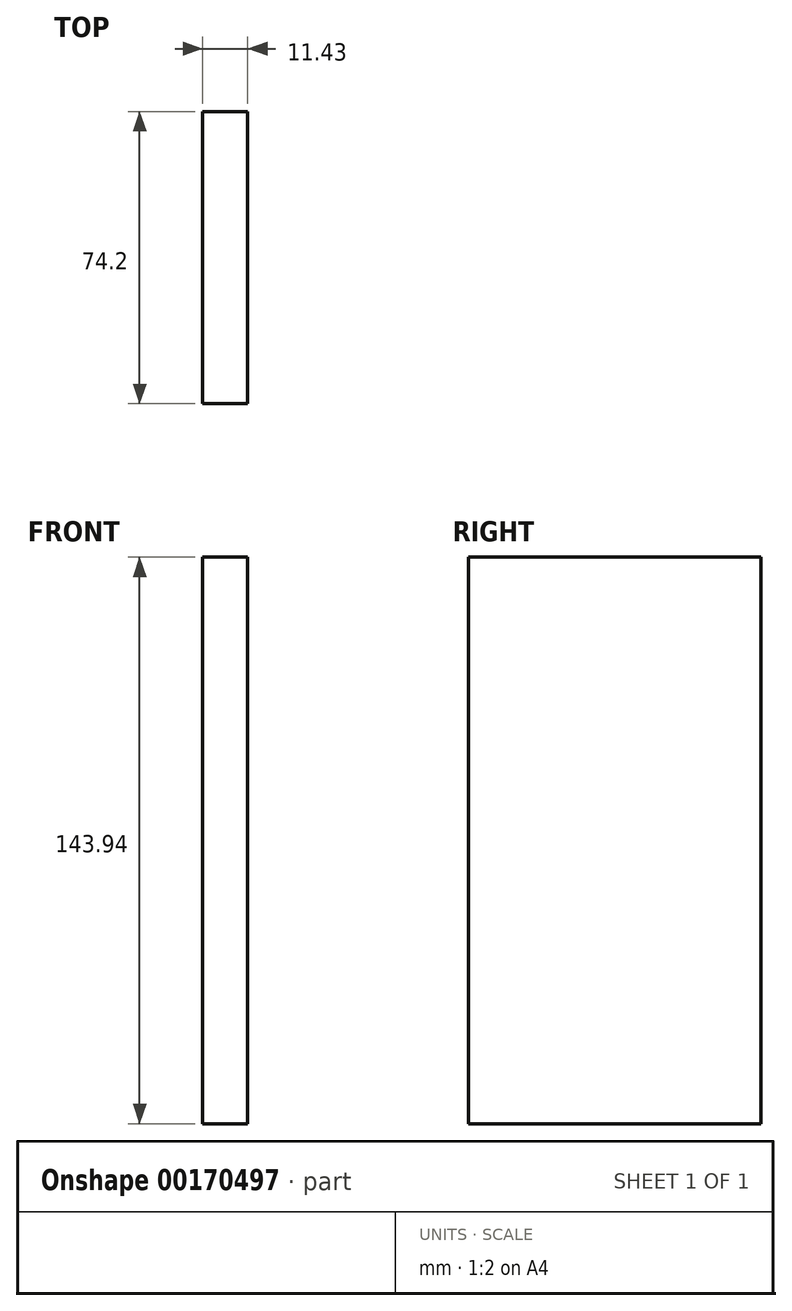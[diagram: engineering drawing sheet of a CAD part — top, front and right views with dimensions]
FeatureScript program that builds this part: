
annotation { "Feature Type Name" : "Feature", "Feature Type Description" : "" }
export const myFeature = defineFeature(function(context is Context, id is Id, definition is map)
    precondition{}
    {
        {
            var Q0;
            Q0=qCreatedBy(makeId("Right.planeOp"),FACE);
            var sketch = newSketch(context, id + "F0", { "sketchPlane" : qUnion([Q0])});
            skLineSegment(sketch, "E0.bottom", {"start": v(-48.16, 60.8) * mm, "end": v(26.04, 60.8) * mm});
            skLineSegment(sketch, "E0.top", {"start": v(-48.16, -83.14) * mm, "end": v(26.04, -83.14) * mm});
            skLineSegment(sketch, "E0.left", {"start": v(-48.16, 60.8) * mm, "end": v(-48.16, -83.14) * mm});
            skLineSegment(sketch, "E0.right", {"start": v(26.04, 60.8) * mm, "end": v(26.04, -83.14) * mm});
            skSolve(sketch);
        }
        {
            var Q0;
            Q0=makeQuery(id+"F0.imprint","IMPRINT",FACE,{"disambiguationData":[TD([[makeQuery(id+"F0.imprint","IMPRINT",EDGE,{"derivedFrom":sQuery(id+"F0.wireOp",EDGE,"E0.bottom")}),-1.0]])]});
            extrude(context, id + "F1", {"entities" : qUnion([Q0]), "depth" : 11.43 * mm});
        }
    });
